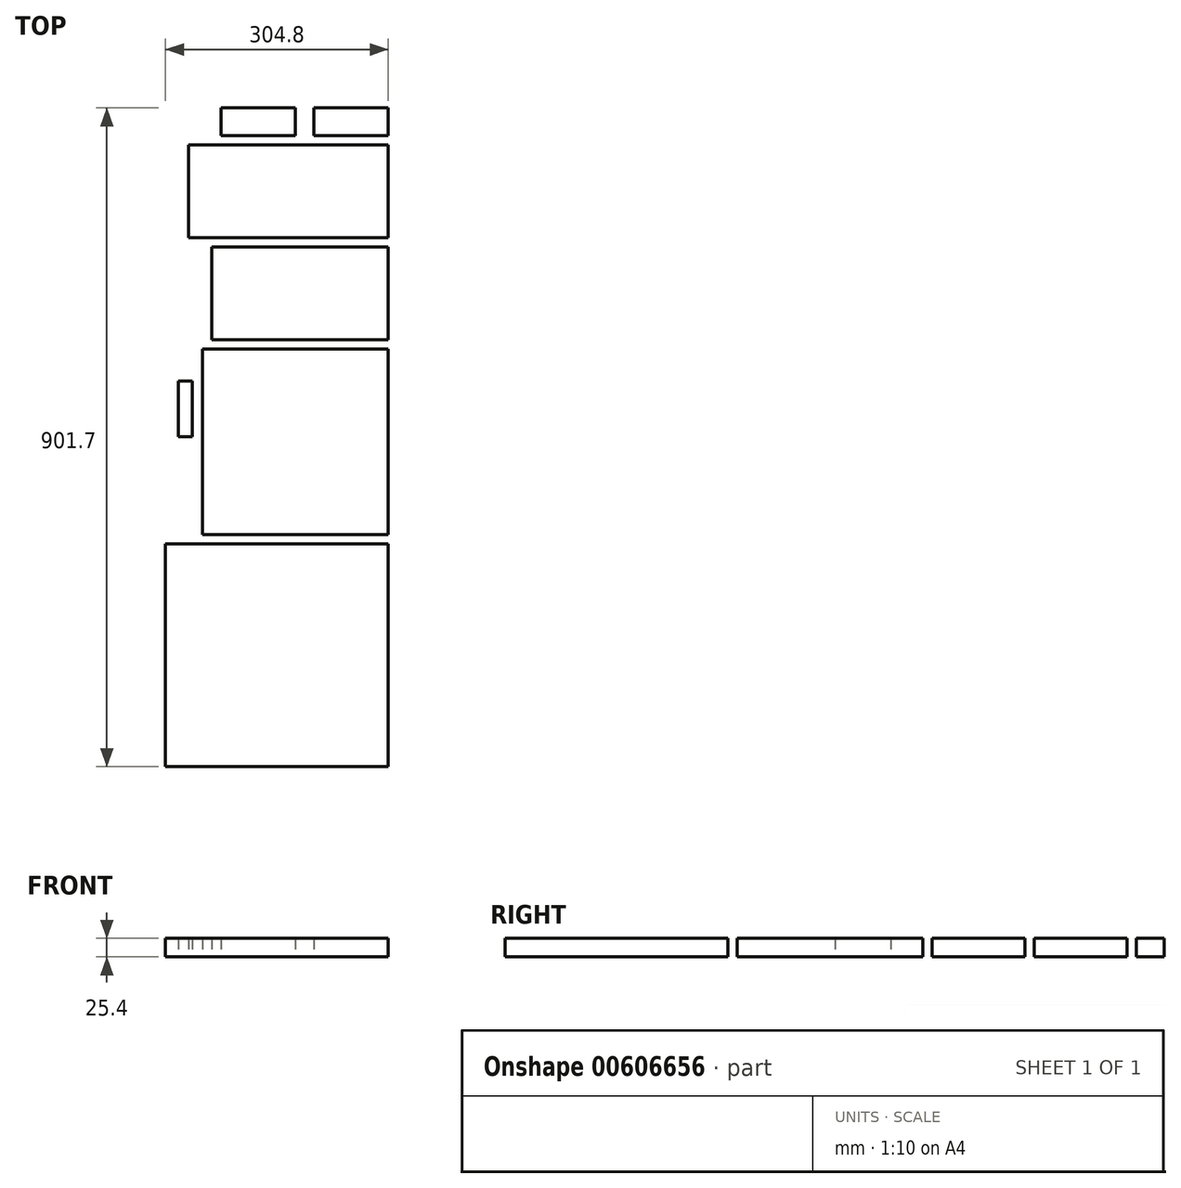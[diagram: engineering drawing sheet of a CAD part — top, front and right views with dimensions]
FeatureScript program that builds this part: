
annotation { "Feature Type Name" : "Feature", "Feature Type Description" : "" }
export const myFeature = defineFeature(function(context is Context, id is Id, definition is map)
    precondition{}
    {
        {
            var Q0;
            Q0=qCreatedBy(makeId("Top.planeOp"),FACE);
            var sketch = newSketch(context, id + "F0", { "sketchPlane" : qUnion([Q0])});
            skLineSegment(sketch, "E0.bottom", {"start": v(-243.83, 1201) * mm, "end": v(60.97, 1201) * mm});
            skLineSegment(sketch, "E0.top", {"start": v(-243.83, -18.2) * mm, "end": v(60.97, -18.2) * mm});
            skLineSegment(sketch, "E0.left", {"start": v(-243.83, 1201) * mm, "end": v(-243.83, -18.2) * mm});
            skLineSegment(sketch, "E0.right", {"start": v(60.97, 1201) * mm, "end": v(60.97, -18.2) * mm});
            skLineSegment(sketch, "E1.bottom", {"start": v(-193.03, 552.61) * mm, "end": v(60.97, 552.61) * mm});
            skLineSegment(sketch, "E1.top", {"start": v(-193.03, 298.61) * mm, "end": v(60.97, 298.61) * mm});
            skLineSegment(sketch, "E1.left", {"start": v(-193.03, 552.61) * mm, "end": v(-193.03, 298.61) * mm});
            skLineSegment(sketch, "E1.right", {"start": v(60.97, 552.61) * mm, "end": v(60.97, 298.61) * mm});
            skLineSegment(sketch, "E2.bottom", {"start": v(60.97, -18.89) * mm, "end": v(-243.83, -18.89) * mm});
            skLineSegment(sketch, "E2.top", {"start": v(60.97, 285.91) * mm, "end": v(-243.83, 285.91) * mm});
            skLineSegment(sketch, "E2.left", {"start": v(60.97, -18.89) * mm, "end": v(60.97, 285.91) * mm});
            skLineSegment(sketch, "E2.right", {"start": v(-243.83, -18.89) * mm, "end": v(-243.83, 285.91) * mm});
            skLineSegment(sketch, "E3.bottom", {"start": v(-40.63, 882.81) * mm, "end": v(60.97, 882.81) * mm});
            skLineSegment(sketch, "E3.top", {"start": v(-40.63, 844.71) * mm, "end": v(60.97, 844.71) * mm});
            skLineSegment(sketch, "E3.left", {"start": v(-40.63, 882.81) * mm, "end": v(-40.63, 844.71) * mm});
            skLineSegment(sketch, "E3.right", {"start": v(60.97, 882.81) * mm, "end": v(60.97, 844.71) * mm});
            skLineSegment(sketch, "E4.bottom", {"start": v(-167.63, 882.81) * mm, "end": v(-66.03, 882.81) * mm});
            skLineSegment(sketch, "E4.top", {"start": v(-167.63, 844.71) * mm, "end": v(-66.03, 844.71) * mm});
            skLineSegment(sketch, "E4.left", {"start": v(-167.63, 882.81) * mm, "end": v(-167.63, 844.71) * mm});
            skLineSegment(sketch, "E4.right", {"start": v(-66.03, 882.81) * mm, "end": v(-66.03, 844.71) * mm});
            skLineSegment(sketch, "E5.bottom", {"start": v(-212.31, 832.01) * mm, "end": v(60.97, 832.01) * mm});
            skLineSegment(sketch, "E5.top", {"start": v(-212.31, 705.01) * mm, "end": v(60.97, 705.01) * mm});
            skLineSegment(sketch, "E5.left", {"start": v(-212.31, 832.01) * mm, "end": v(-212.31, 705.01) * mm});
            skLineSegment(sketch, "E5.right", {"start": v(60.97, 832.01) * mm, "end": v(60.97, 705.01) * mm});
            skLineSegment(sketch, "E6.bottom", {"start": v(-180.33, 692.31) * mm, "end": v(60.97, 692.31) * mm});
            skLineSegment(sketch, "E6.top", {"start": v(-180.33, 565.31) * mm, "end": v(60.97, 565.31) * mm});
            skLineSegment(sketch, "E6.left", {"start": v(-180.33, 692.31) * mm, "end": v(-180.33, 565.31) * mm});
            skLineSegment(sketch, "E6.right", {"start": v(60.97, 692.31) * mm, "end": v(60.97, 565.31) * mm});
            skLineSegment(sketch, "E7.bottom", {"start": v(-225.98, 432.62) * mm, "end": v(-206.93, 432.62) * mm});
            skLineSegment(sketch, "E7.top", {"start": v(-225.98, 508.82) * mm, "end": v(-206.93, 508.82) * mm});
            skLineSegment(sketch, "E7.left", {"start": v(-225.98, 432.62) * mm, "end": v(-225.98, 508.82) * mm});
            skLineSegment(sketch, "E7.right", {"start": v(-206.93, 432.62) * mm, "end": v(-206.93, 508.82) * mm});
            skSolve(sketch);
        }
        {
            var Q0;
            {var subQ0=sQuery(id+"F0.wireOp",EDGE,"E0.top");Q0=makeQuery(id+"F0.imprint","IMPRINT",FACE,{"disambiguationData":[TD([[makeQuery(id+"F0.imprint","IMPRINT",EDGE,{"derivedFrom":subQ0}),-1.0]])]});}
            var Q1;
            {var subQ0=sQuery(id+"F0.wireOp",EDGE,"E0.top");Q1=makeQuery(id+"F0.imprint","IMPRINT",FACE,{"disambiguationData":[TD([[makeQuery(id+"F0.imprint","IMPRINT",EDGE,{"derivedFrom":subQ0}),1.0]])]});}
            var Q2;
            Q2=makeQuery(id+"F0.imprint","IMPRINT",FACE,{"disambiguationData":[TD([[makeQuery(id+"F0.imprint","IMPRINT",EDGE,{"derivedFrom":sQuery(id+"F0.wireOp",EDGE,"E1.bottom")}),-1.0]])]});
            var Q3;
            Q3=makeQuery(id+"F0.imprint","IMPRINT",FACE,{"disambiguationData":[TD([[makeQuery(id+"F0.imprint","IMPRINT",EDGE,{"derivedFrom":sQuery(id+"F0.wireOp",EDGE,"E6.bottom")}),-1.0]])]});
            var Q4;
            Q4=makeQuery(id+"F0.imprint","IMPRINT",FACE,{"disambiguationData":[TD([[makeQuery(id+"F0.imprint","IMPRINT",EDGE,{"derivedFrom":sQuery(id+"F0.wireOp",EDGE,"E5.bottom")}),-1.0]])]});
            var Q5;
            Q5=makeQuery(id+"F0.imprint","IMPRINT",FACE,{"disambiguationData":[TD([[makeQuery(id+"F0.imprint","IMPRINT",EDGE,{"derivedFrom":sQuery(id+"F0.wireOp",EDGE,"E4.bottom")}),-1.0]])]});
            var Q6;
            Q6=makeQuery(id+"F0.imprint","IMPRINT",FACE,{"disambiguationData":[TD([[makeQuery(id+"F0.imprint","IMPRINT",EDGE,{"derivedFrom":sQuery(id+"F0.wireOp",EDGE,"E3.bottom")}),-1.0]])]});
            var Q7;
            Q7=makeQuery(id+"F0.imprint","IMPRINT",FACE,{"disambiguationData":[TD([[makeQuery(id+"F0.imprint","IMPRINT",EDGE,{"derivedFrom":sQuery(id+"F0.wireOp",EDGE,"E7.bottom")}),1.0]])]});
            extrude(context, id + "F1", {"entities" : qUnion([Q0, Q1, Q2, Q3, Q4, Q5, Q6, Q7]), "depth" : 25.4 * mm, "offsetDistance" : 25.4 * mm});
        }
    });
